# Revit family: Electronics_Visual-TVs_ViewSonic_ViewSonicR-EP3220T-Digital-Billboard-Display
name_source: partatom
category: Electrical Equipment
revit_build: Autodesk Revit 2017 (Build: 20190508_0315(x64)
units: mm (PartAtom-declared; Revit-internal decimal feet)

## family parameters
Always vertical = Yes
Cut with Voids When Loaded = No
OmniClass Number = 23.85.10.14.24.17
OmniClass Title = Plasma Video Monitors
Panel Configuration = Two Columns, Circuits Across
Part Type = Panelboard
Room Calculation Point = No
Round Connector Dimension = Use Diameter
Shared = No
Work Plane-Based = No

## types (1)
- EP 3220 T
    Aspect Ratio = 16:9
    Assembly Code = D5030500
    Backlight = WLED
    Backlight Life = 30,000 hrs
    Brightness = 300 cd/m2
    Colors = 16.7M colors
    Contrast Ratio = 1200:1
    Cover Material = Plastic - ViewSonic - Black
    Covering Color = Plastic - ViewSonic - Black
    Description = EP3220T - 32" Display, 300 cd/m2 Brightness, Integrated Media Player

The ViewSonic® EP3220T is a 32" all-in-one digital billboard with 10-point interactive touch. Great for grabbing attention in busy, high-traffic areas, the interactive EP3220T comes with a scratch-proof tempered glass faceplate for durability in public spaces. Featuring Full HD 1080p resolution, 178°/178° wide-angle viewing, and 300-nit brightness, the EP3220T delivers customized multimedia messaging with vivid clarity. Photo and video files can be played back using the embedded Quad-core media player and 16GB of internal memory, or add your own media player utilizing the the convenient HDMI or RGB inputs.
    Display Area (mm) = 698.4(H) x 392.85(V)
    Display Size = 32"
    Edition number = 1
    Keynote = 11130
    Light Source = ELED
    Manufacturer = ViewSonic
    Model = viewsonic_ep3220t
    Orientation = Landscape / Portrait
    Panel Size = 32"
    Product Guid = f197385e-efe8-4a52-a7f8-3a357e0e1a8c
    Product data url = https://www.bimobject.com
    Resolution = 1920 x 1080; 16:9
    Response Time = 8 ms(typ.)
    Screen Material = Screen - ViewSonic - WP3220
    Surface Treatment = Anti-glare, Hard coating (3H)
    URL = https://www.viewsonic.com
    Viewable Area (In.) = 32"
    Viewing Angles = H = 178, V = 178 typ.

## geometry (parser evidence)
native form markers: Sweep x5
no freeform markers — native parametric forms only
